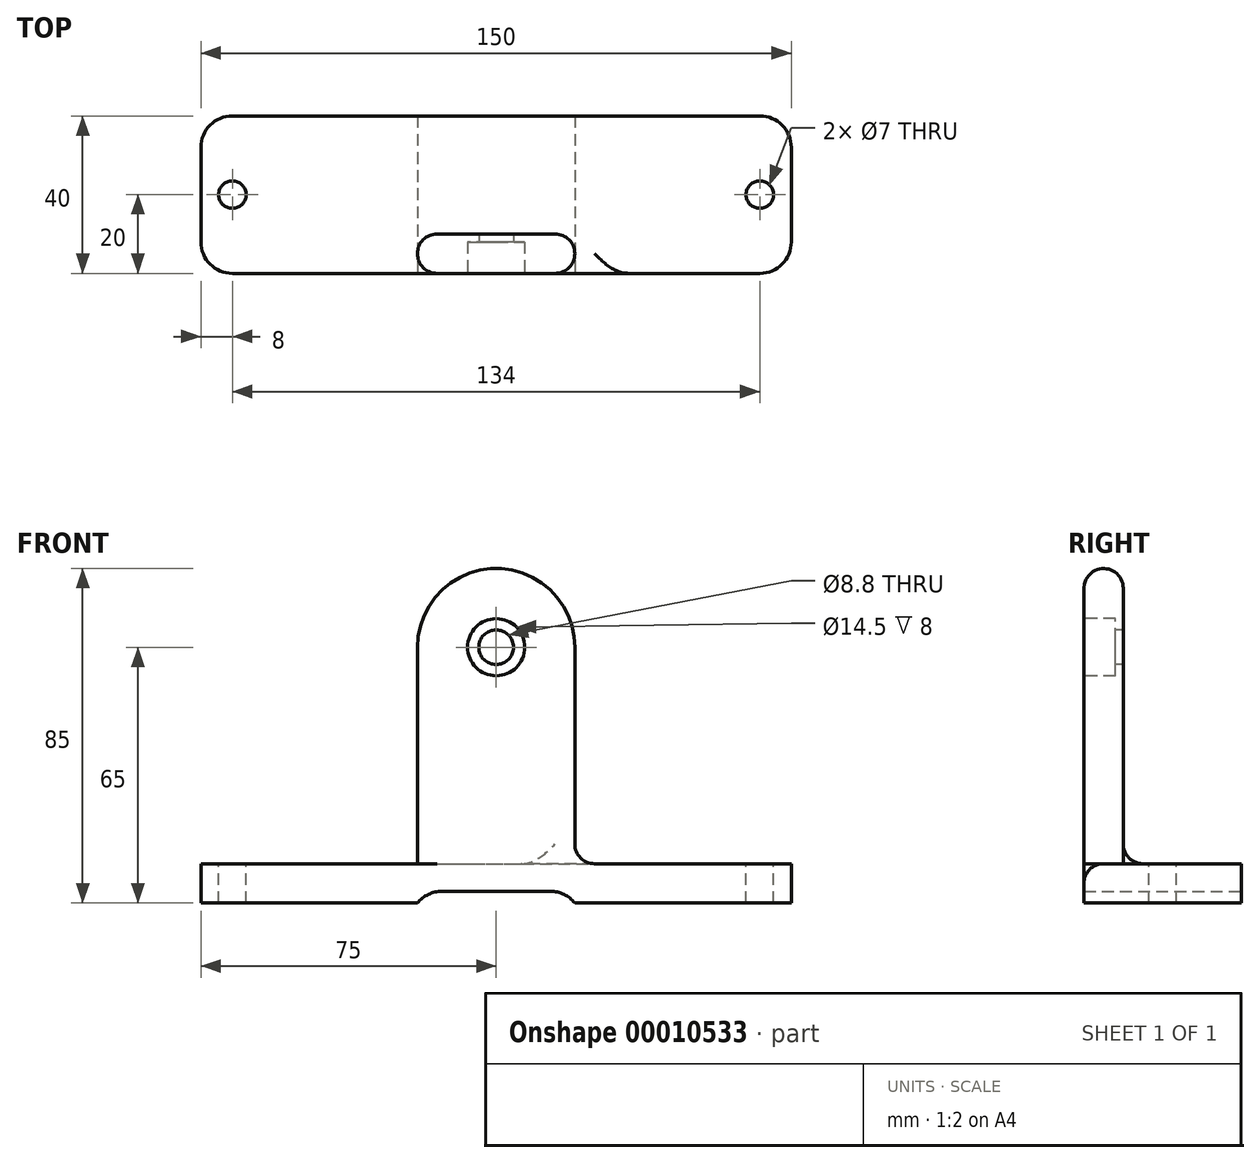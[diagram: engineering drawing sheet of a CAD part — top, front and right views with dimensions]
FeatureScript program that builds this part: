
annotation { "Feature Type Name" : "Feature", "Feature Type Description" : "" }
export const myFeature = defineFeature(function(context is Context, id is Id, definition is map)
    precondition{}
    {
        {
            var Q0;
            Q0=qCreatedBy(makeId("Top.planeOp"),FACE);
            var sketch = newSketch(context, id + "F0", { "sketchPlane" : qUnion([Q0])});
            skLineSegment(sketch, "E0.bottom", {"start": v(0, 0) * mm, "end": v(150, 0) * mm});
            skLineSegment(sketch, "E0.top", {"start": v(0, 40) * mm, "end": v(150, 40) * mm});
            skLineSegment(sketch, "E0.left", {"start": v(0, 0) * mm, "end": v(0, 40) * mm});
            skLineSegment(sketch, "E0.right", {"start": v(150, 0) * mm, "end": v(150, 40) * mm});
            skSolve(sketch);
        }
        {
            var Q0;
            Q0=qSketchRegion(id+"F0",true);
            extrude(context, id + "F1", {"entities" : qUnion([Q0]), "depth" : 10 * mm});
        }
        {
            var Q0;
            Q0=makeQuery(id+"F1.opExtrude","SWEPT_FACE",FACE,{"disambiguationData":[OSD([sQuery(id+"F0.wireOp",EDGE,"E0.bottom")])]});
            var sketch = newSketch(context, id + "F2", { "sketchPlane" : qUnion([Q0])});
            skLineSegment(sketch, "E1", {"start": v(55, 0) * mm, "end": v(55, 65) * mm});
            skArc(sketch, "E2", {"start": v(55, 65) * mm, "mid": v(75, 85) * mm, "end": v(95, 65) * mm});
            skLineSegment(sketch, "E3", {"start": v(95, 65) * mm, "end": v(95, 0) * mm});
            skLineSegment(sketch, "E4", {"start": v(95, 0) * mm, "end": v(55, 0) * mm});
            skSolve(sketch);
        }
        {
            var Q0;
            Q0=qSketchRegion(id+"F2",true);
            extrude(context, id + "F3", {"entities" : qUnion([Q0]), "operationType" : NewBodyOperationType.ADD, "oppositeDirection" : true, "depth" : 10 * mm});
        }
        {
            var Q0;
            Q0=makeQuery(id+"F3.boolean.opBoolean","MERGE",FACE,{"derivedFrom":[makeQuery(id+"F1.opExtrude","SWEPT_FACE",FACE,{"disambiguationData":[OSD([sQuery(id+"F0.wireOp",EDGE,"E0.bottom")])]}),makeQuery(id+"F3.opExtrude","CAP_FACE",FACE,{"disambiguationData":[OSD([sQuery(id+"F2.wireOp",EDGE,"E1"),sQuery(id+"F2.wireOp",EDGE,"E2"),sQuery(id+"F2.wireOp",EDGE,"E3"),sQuery(id+"F2.wireOp",EDGE,"E4")])],"isStart":true})]});
            var sketch = newSketch(context, id + "F4", { "sketchPlane" : qUnion([Q0])});
            skLineSegment(sketch, "E5.bottom", {"start": v(55, 0) * mm, "end": v(95, 0) * mm});
            skLineSegment(sketch, "E5.top", {"start": v(55, 3) * mm, "end": v(95, 3) * mm});
            skLineSegment(sketch, "E5.left", {"start": v(55, 0) * mm, "end": v(55, 3) * mm});
            skLineSegment(sketch, "E5.right", {"start": v(95, 0) * mm, "end": v(95, 3) * mm});
            skSolve(sketch);
        }
        {
            var Q0;
            Q0=qSketchRegion(id+"F4",true);
            extrude(context, id + "F5", {"entities" : qUnion([Q0]), "operationType" : NewBodyOperationType.REMOVE, "endBound" : BoundingType.THROUGH_ALL, "oppositeDirection" : true, "depth" : 25 * mm});
        }
        {
            var Q0;
            Q0=makeQuery(id+"F3.boolean.opBoolean","MERGE",FACE,{"derivedFrom":[makeQuery(id+"F1.opExtrude","SWEPT_FACE",FACE,{"disambiguationData":[OSD([sQuery(id+"F0.wireOp",EDGE,"E0.bottom")])]}),makeQuery(id+"F3.opExtrude","CAP_FACE",FACE,{"disambiguationData":[OSD([sQuery(id+"F2.wireOp",EDGE,"E1"),sQuery(id+"F2.wireOp",EDGE,"E2"),sQuery(id+"F2.wireOp",EDGE,"E3"),sQuery(id+"F2.wireOp",EDGE,"E4")])],"isStart":true})]});
            var sketch = newSketch(context, id + "F6", { "sketchPlane" : qUnion([Q0])});
            skCircle(sketch, "E6", {"center": v(75, 65) * mm, "radius": 4.4 * mm});
            skSolve(sketch);
        }
        {
            var Q0;
            Q0=qSketchRegion(id+"F6",true);
            extrude(context, id + "F7", {"entities" : qUnion([Q0]), "operationType" : NewBodyOperationType.REMOVE, "endBound" : BoundingType.THROUGH_ALL, "oppositeDirection" : true, "depth" : 25 * mm});
        }
        {
            var Q0;
            Q0=makeQuery(id+"F3.boolean.opBoolean","MERGE",FACE,{"derivedFrom":[makeQuery(id+"F1.opExtrude","SWEPT_FACE",FACE,{"disambiguationData":[OSD([sQuery(id+"F0.wireOp",EDGE,"E0.bottom")])]}),makeQuery(id+"F3.opExtrude","CAP_FACE",FACE,{"disambiguationData":[OSD([sQuery(id+"F2.wireOp",EDGE,"E1"),sQuery(id+"F2.wireOp",EDGE,"E2"),sQuery(id+"F2.wireOp",EDGE,"E3"),sQuery(id+"F2.wireOp",EDGE,"E4")])],"isStart":true})]});
            var sketch = newSketch(context, id + "F8", { "sketchPlane" : qUnion([Q0])});
            skCircle(sketch, "E7", {"center": v(75, 65) * mm, "radius": 7.25 * mm});
            skSolve(sketch);
        }
        {
            var Q0;
            Q0=qSketchRegion(id+"F8",true);
            extrude(context, id + "F9", {"entities" : qUnion([Q0]), "operationType" : NewBodyOperationType.REMOVE, "oppositeDirection" : true, "depth" : 8 * mm});
        }
        {
            var Q0;
            Q0=makeQuery(id+"F5.boolean.opBoolean","COPY",EDGE,{"derivedFrom":makeQuery(id+"F5.opExtrude","SWEPT_EDGE",EDGE,{"disambiguationData":[OSD([sQuery(id+"F4.wireOp",EDGE,"E5.top"),sQuery(id+"F4.wireOp",EDGE,"E5.left")])]})});
            var Q1;
            Q1=makeQuery(id+"F5.boolean.opBoolean","COPY",EDGE,{"derivedFrom":makeQuery(id+"F5.opExtrude","SWEPT_EDGE",EDGE,{"disambiguationData":[OSD([sQuery(id+"F4.wireOp",EDGE,"E5.top"),sQuery(id+"F4.wireOp",EDGE,"E5.right")])]})});
            var Q2;
            Q2=makeQuery(id+"F1.opExtrude","SWEPT_EDGE",EDGE,{"disambiguationData":[OSD([sQuery(id+"F0.wireOp",EDGE,"E0.bottom"),sQuery(id+"F0.wireOp",EDGE,"E0.right")])]});
            var Q3;
            Q3=makeQuery(id+"F1.opExtrude","SWEPT_EDGE",EDGE,{"disambiguationData":[OSD([sQuery(id+"F0.wireOp",EDGE,"E0.bottom"),sQuery(id+"F0.wireOp",EDGE,"E0.left")])]});
            var Q4;
            Q4=makeQuery(id+"F1.opExtrude","SWEPT_EDGE",EDGE,{"disambiguationData":[OSD([sQuery(id+"F0.wireOp",EDGE,"E0.top"),sQuery(id+"F0.wireOp",EDGE,"E0.left")])]});
            var Q5;
            Q5=makeQuery(id+"F1.opExtrude","SWEPT_EDGE",EDGE,{"disambiguationData":[OSD([sQuery(id+"F0.wireOp",EDGE,"E0.top"),sQuery(id+"F0.wireOp",EDGE,"E0.right")])]});
            fillet(context, id + "F10", {"entities" : qUnion([Q0, Q1, Q2, Q3, Q4, Q5]), "radius" : 8 * mm, "tangentPropagation" : true, "allowEdgeOverflow" : false});
        }
        {
            var Q0;
            Q0=makeQuery(id+"F1.opExtrude","CAP_FACE",FACE,{"disambiguationData":[OSD([sQuery(id+"F0.wireOp",EDGE,"E0.bottom"),sQuery(id+"F0.wireOp",EDGE,"E0.top"),sQuery(id+"F0.wireOp",EDGE,"E0.left"),sQuery(id+"F0.wireOp",EDGE,"E0.right")])],"isStart":false});
            var sketch = newSketch(context, id + "F11", { "sketchPlane" : qUnion([Q0])});
            skCircle(sketch, "E8", {"center": v(8, 20) * mm, "radius": 3.5 * mm});
            skCircle(sketch, "E9", {"center": v(142, 20) * mm, "radius": 3.5 * mm});
            skSolve(sketch);
        }
        {
            var Q0;
            Q0=qSketchRegion(id+"F11",true);
            extrude(context, id + "F12", {"entities" : qUnion([Q0]), "operationType" : NewBodyOperationType.REMOVE, "endBound" : BoundingType.THROUGH_ALL, "oppositeDirection" : true, "depth" : 25 * mm});
        }
        {
            var Q0;
            Q0=makeQuery(id+"F3.opExtrude","CAP_EDGE",EDGE,{"disambiguationData":[OSD([sQuery(id+"F2.wireOp",EDGE,"E2")])],"isStart":false});
            var Q1;
            Q1=makeQuery(id+"F3.opExtrude","CAP_EDGE",EDGE,{"disambiguationData":[OSD([sQuery(id+"F2.wireOp",EDGE,"E2")])],"isStart":true});
            var Q2;
            Q2=makeQuery(id+"F3.opExtrude","CAP_EDGE",EDGE,{"disambiguationData":[OSD([sQuery(id+"F2.wireOp",EDGE,"E3")])],"isStart":true});
            var Q3;
            Q3=makeQuery(id+"F3.boolean.opBoolean","INTERSECT",EDGE,{"derivedFrom":[makeQuery(id+"F1.opExtrude","CAP_FACE",FACE,{"disambiguationData":[OSD([sQuery(id+"F0.wireOp",EDGE,"E0.bottom"),sQuery(id+"F0.wireOp",EDGE,"E0.top"),sQuery(id+"F0.wireOp",EDGE,"E0.left"),sQuery(id+"F0.wireOp",EDGE,"E0.right")])],"isStart":false}),makeQuery(id+"F3.opExtrude","SWEPT_FACE",FACE,{"disambiguationData":[OSD([sQuery(id+"F2.wireOp",EDGE,"E3")])]})]});
            fillet(context, id + "F13", {"entities" : qUnion([Q0, Q1, Q2, Q3]), "radius" : 5 * mm, "tangentPropagation" : true, "allowEdgeOverflow" : false});
        }
    });
